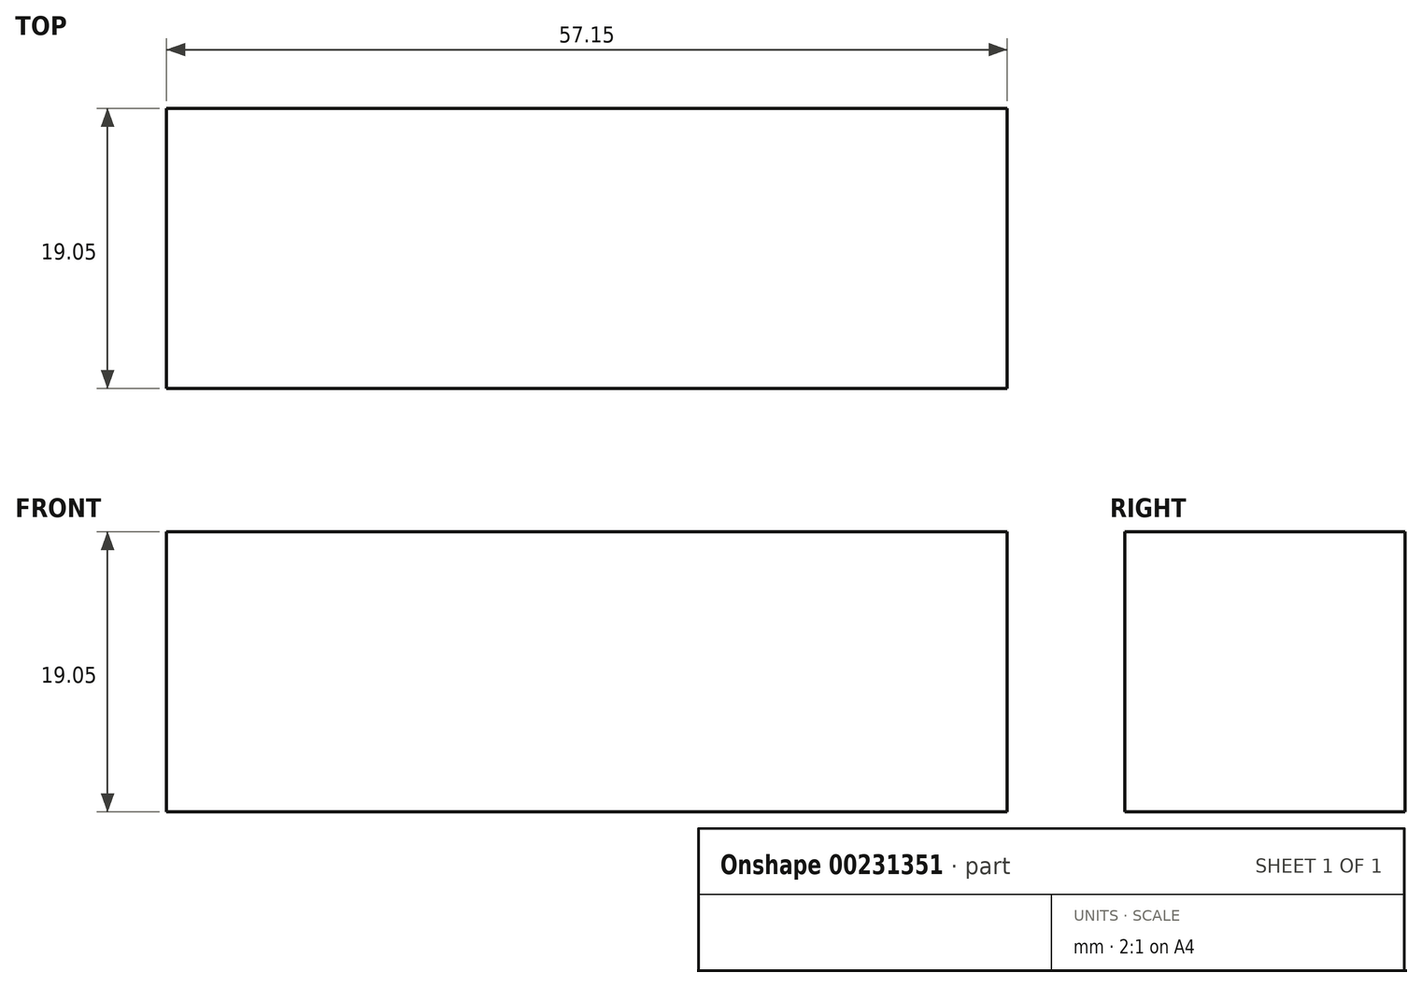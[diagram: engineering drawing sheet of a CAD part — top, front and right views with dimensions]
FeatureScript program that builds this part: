
annotation { "Feature Type Name" : "Feature", "Feature Type Description" : "" }
export const myFeature = defineFeature(function(context is Context, id is Id, definition is map)
    precondition{}
    {
        {
            var Q0;
            Q0=qCreatedBy(makeId("Front.planeOp"),FACE);
            var sketch = newSketch(context, id + "F0", { "sketchPlane" : qUnion([Q0])});
            skLineSegment(sketch, "E0.bottom", {"start": v(0, 0) * mm, "end": v(-57.15, 0) * mm});
            skLineSegment(sketch, "E0.top", {"start": v(0, 19.05) * mm, "end": v(-57.15, 19.05) * mm});
            skLineSegment(sketch, "E0.left", {"start": v(0, 0) * mm, "end": v(0, 19.05) * mm});
            skLineSegment(sketch, "E0.right", {"start": v(-57.15, 0) * mm, "end": v(-57.15, 19.05) * mm});
            skLineSegment(sketch, "E1.bottom", {"start": v(-19.05, 0) * mm, "end": v(0, 0) * mm});
            skLineSegment(sketch, "E1.top", {"start": v(-19.05, -19.05) * mm, "end": v(0, -19.05) * mm});
            skLineSegment(sketch, "E1.left", {"start": v(-19.05, 0) * mm, "end": v(-19.05, -19.05) * mm});
            skLineSegment(sketch, "E1.right", {"start": v(0, 0) * mm, "end": v(0, -19.05) * mm});
            skSolve(sketch);
        }
        {
            var Q0;
            Q0=makeQuery(id+"F0.imprint","IMPRINT",FACE,{"disambiguationData":[TD([[makeQuery(id+"F0.imprint","IMPRINT",EDGE,{"derivedFrom":sQuery(id+"F0.wireOp",EDGE,"E0.bottom")}),-1.0]])]});
            var Q1;
            Q1=makeQuery(id+"F0.imprint","IMPRINT",FACE,{"disambiguationData":[TD([[makeQuery(id+"F0.imprint","IMPRINT",EDGE,{"derivedFrom":sQuery(id+"F0.wireOp",EDGE,"E1.bottom")}),-1.0]])]});
            extrude(context, id + "F1", {"entities" : qUnion([Q0, Q1]), "depth" : 19.05 * mm});
        }
    });
